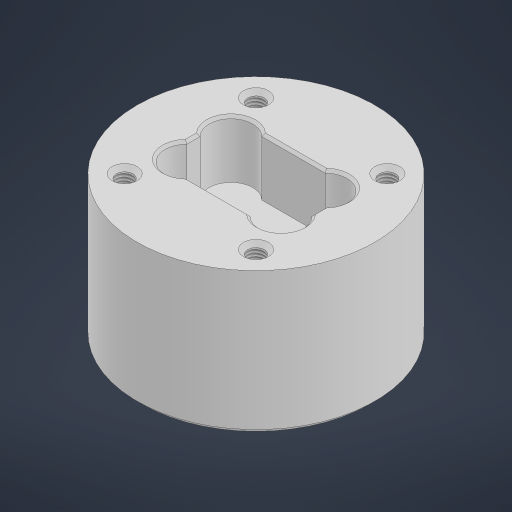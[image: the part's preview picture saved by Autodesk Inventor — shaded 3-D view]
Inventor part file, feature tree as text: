
AUTODESK INVENTOR PART (.ipt)
format: ipt  version: 2024.3 (Build 283343000, 343)  size: 421,376 bytes
history: native  units: mm
features: sketch x3, extrude x3, chamfer x2, hole x1, other x1, projected_geometry x1
ambient origin geometry x8: Origin, YZ Plane, XZ Plane, XY Plane, X Axis, Y Axis, Z Axis, Center Point
bodies: Solid1 (feature_tree)
feature tree (11):
  sketch  "Sketch1"  dims[d0=30.0mm d2=95.0mm]
  extrude  "Extrusion1"  Depth=95.0mm
  extrude  "Extrusion2"  Depth=57.0mm TaperAngle=0.0deg
  extrude  "Extrusion3"  Depth=1.0mm TaperAngle=45.0deg
  hole  "Hole1"  [1 undecoded]
  chamfer  "Chamfer1"  Distance=4.0mm
  chamfer  "Chamfer2"  Distance=30.0mm
  other  "Mark1"
  sketch  "Sketch2"  dims[d5=57.0mm d6=0.0mm d7=23.0mm d8=0.0mm]
  sketch  "Sketch3"  dims[d9=6.647mm d10=18.0mm d11=10.0mm d12=2.0mm d13=90.0deg d14=17.0mm d15=20.594885mm d17=1.0mm d18=2.0mm d19=45.0deg d20=2.0mm d21=2.0mm d22=45.0deg d23=4.0mm d24=30.0mm d27=50.0mm d33=45.0deg d34=17.5mm d35=23.0mm d36=0.0mm]
  projected_geometry  "Projected Loop1"
note: 1 required parameter value undecoded (feature->parameter linkage not recoverable at this tier; creation-order binding heuristic only, values carry confidence <= 0.55)
